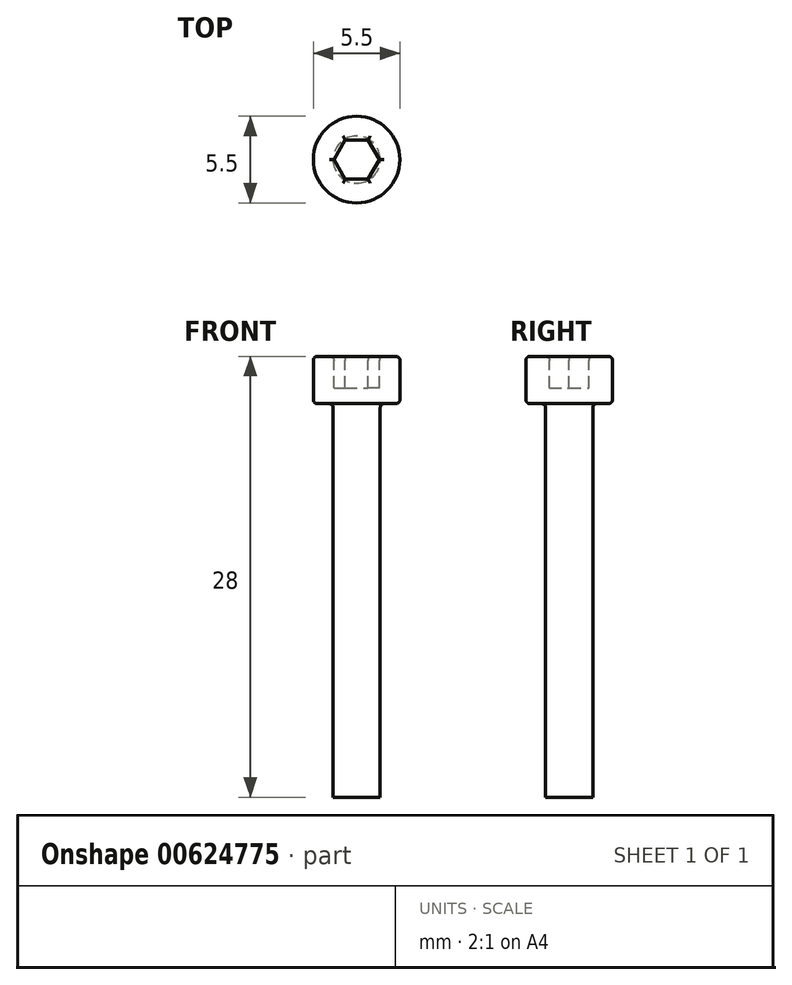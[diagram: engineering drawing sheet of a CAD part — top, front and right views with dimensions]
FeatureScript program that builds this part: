
annotation { "Feature Type Name" : "Feature", "Feature Type Description" : "" }
export const myFeature = defineFeature(function(context is Context, id is Id, definition is map)
    precondition{}
    {
        {
            var Q0;
            Q0=qCreatedBy(makeId("Top.planeOp"),FACE);
            var sketch = newSketch(context, id + "F0", { "sketchPlane" : qUnion([Q0])});
            skCircle(sketch, "E0", {"center": v(0, 0) * mm, "radius": 2.75 * mm});
            skSolve(sketch);
        }
        {
            var Q0;
            Q0 = qSketchRegion(id + "F0", true);
            extrude(context, id + "F1", {"entities" : qUnion([Q0]), "oppositeDirection" : true, "depth" : 3 * mm, "offsetDistance" : 25 * mm});
        }
        {
            var Q0;
            Q0=makeQuery(id+"F1.opExtrude","CAP_FACE",FACE,{"disambiguationData":[OSD([sQuery(id+"F0.wireOp",EDGE,"E0")])],"isStart":false});
            var sketch = newSketch(context, id + "F2", { "sketchPlane" : qUnion([Q0])});
            skCircle(sketch, "E1", {"center": v(0, 0) * mm, "radius": 1.5 * mm});
            skSolve(sketch);
        }
        {
            var Q0;
            Q0 = qSketchRegion(id + "F2", true);
            extrude(context, id + "F3", {"entities" : qUnion([Q0]), "operationType" : NewBodyOperationType.ADD, "depth" : 25 * mm, "offsetDistance" : 25 * mm});
        }
        {
            var Q0;
            Q0=makeQuery(id+"F1.opExtrude","CAP_FACE",FACE,{"disambiguationData":[OSD([sQuery(id+"F0.wireOp",EDGE,"E0")])],"isStart":true});
            var sketch = newSketch(context, id + "F4", { "sketchPlane" : qUnion([Q0])});
            skCircle(sketch, "E2.cCircle", {"center": v(0, 0) * mm, "radius": 1.25 * mm, "construction": true});
            skLineSegment(sketch, "E2.0", {"start": v(-0.72, 1.25) * mm, "end": v(0.72, 1.25) * mm});
            skLineSegment(sketch, "E2.1", {"start": v(0.72, 1.25) * mm, "end": v(1.44, 0) * mm});
            skLineSegment(sketch, "E2.2", {"start": v(1.44, 0) * mm, "end": v(0.72, -1.25) * mm});
            skLineSegment(sketch, "E2.3", {"start": v(0.72, -1.25) * mm, "end": v(-0.72, -1.25) * mm});
            skLineSegment(sketch, "E2.4", {"start": v(-0.72, -1.25) * mm, "end": v(-1.44, 0) * mm});
            skLineSegment(sketch, "E2.5", {"start": v(-1.44, 0) * mm, "end": v(-0.72, 1.25) * mm});
            skPoint(sketch, "E2.0.midPoint", {"position": v(0, 1.25) * mm});
            skSolve(sketch);
        }
        {
            var Q0;
            Q0 = qSketchRegion(id + "F4", true);
            extrude(context, id + "F5", {"entities" : qUnion([Q0]), "operationType" : NewBodyOperationType.REMOVE, "oppositeDirection" : true, "depth" : 2 * mm, "offsetDistance" : 25 * mm});
        }
        {
            var Q0;
            Q0=makeQuery(id+"F1.opExtrude","CAP_FACE",FACE,{"disambiguationData":[OSD([sQuery(id+"F0.wireOp",EDGE,"E0")])],"isStart":true});
            var Q1;
            Q1=makeQuery(id+"F1.opExtrude","CAP_FACE",FACE,{"disambiguationData":[OSD([sQuery(id+"F0.wireOp",EDGE,"E0")])],"isStart":false});
            fillet(context, id + "F6", {"entities" : qUnion([Q0, Q1]), "radius" : .25 * mm, "tangentPropagation" : true, "allowEdgeOverflow" : false});
        }
    });
